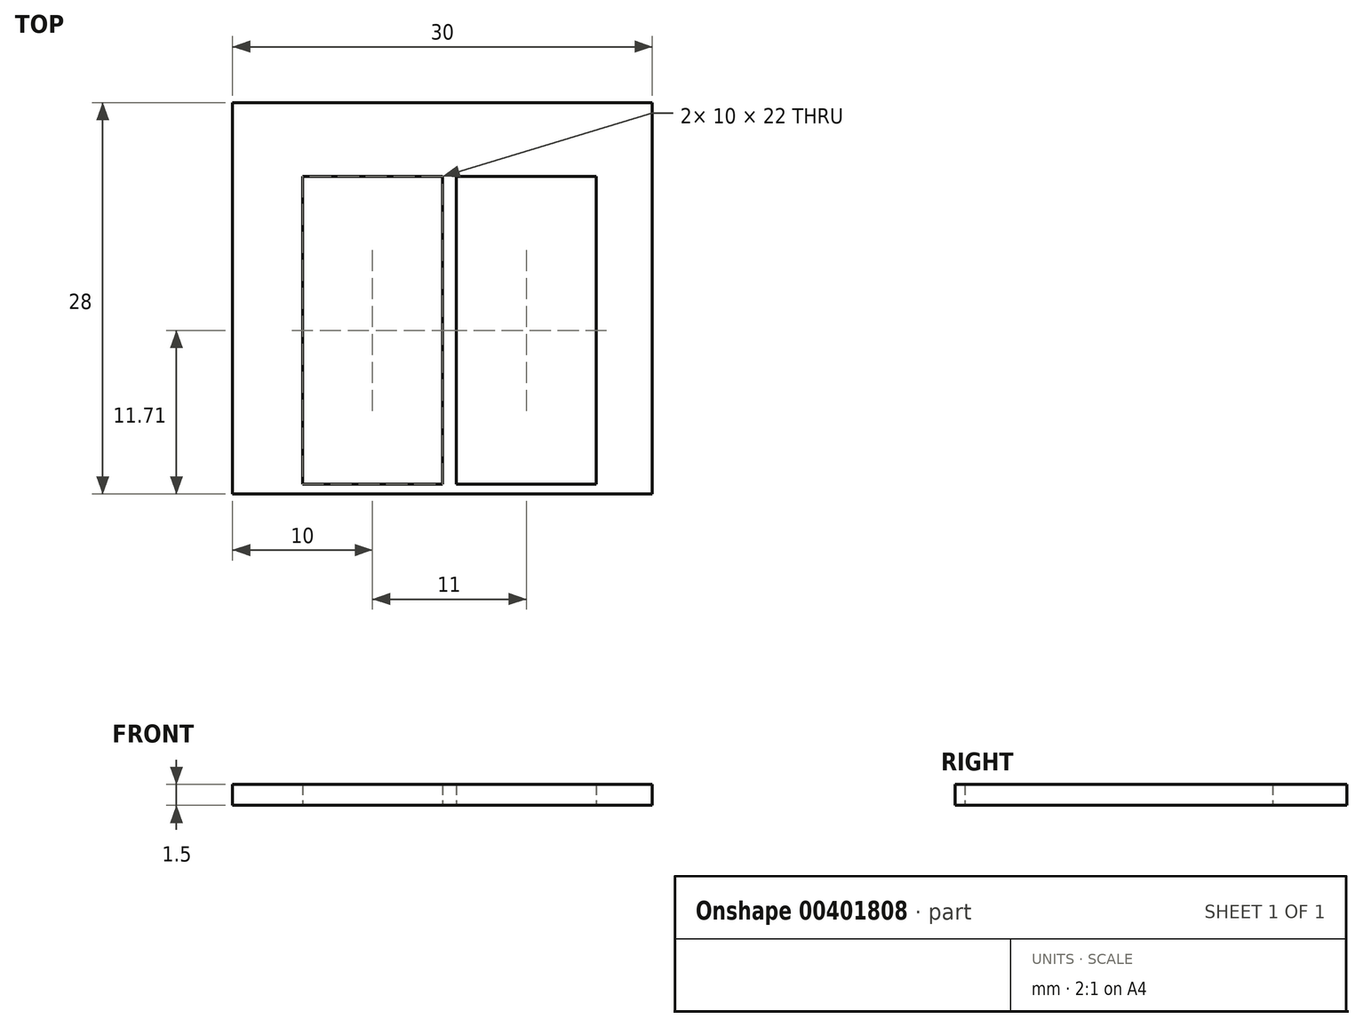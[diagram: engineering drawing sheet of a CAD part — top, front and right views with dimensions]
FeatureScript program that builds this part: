
annotation { "Feature Type Name" : "Feature", "Feature Type Description" : "" }
export const myFeature = defineFeature(function(context is Context, id is Id, definition is map)
    precondition{}
    {
        {
            var Q0;
            Q0=qCreatedBy(makeId("Top.planeOp"),FACE);
            var sketch = newSketch(context, id + "F0", { "sketchPlane" : qUnion([Q0])});
            skLineSegment(sketch, "E0.bottom", {"start": v(0, 0) * mm, "end": v(30, 0) * mm});
            skLineSegment(sketch, "E0.top", {"start": v(0, 28) * mm, "end": v(30, 28) * mm});
            skLineSegment(sketch, "E0.left", {"start": v(0, 0) * mm, "end": v(0, 28) * mm});
            skLineSegment(sketch, "E0.right", {"start": v(30, 0) * mm, "end": v(30, 28) * mm});
            skLineSegment(sketch, "E1.bottom", {"start": v(5, 22.7) * mm, "end": v(15, 22.7) * mm});
            skLineSegment(sketch, "E1.top", {"start": v(5, 0.7) * mm, "end": v(15, 0.7) * mm});
            skLineSegment(sketch, "E1.left", {"start": v(5, 22.7) * mm, "end": v(5, 0.7) * mm});
            skLineSegment(sketch, "E1.right", {"start": v(15, 22.7) * mm, "end": v(15, 0.7) * mm});
            skLineSegment(sketch, "E2.1.0.0", {"start": v(16, 22.7) * mm, "end": v(16, 0.7) * mm});
            skLineSegment(sketch, "E2.1.0.1", {"start": v(16, 22.7) * mm, "end": v(26, 22.7) * mm});
            skLineSegment(sketch, "E2.1.0.2", {"start": v(26, 22.7) * mm, "end": v(26, 0.7) * mm});
            skLineSegment(sketch, "E2.1.0.3", {"start": v(16, 0.7) * mm, "end": v(26, 0.7) * mm});
            skLineSegment(sketch, "E2.direction1", {"start": v(5, 0.7) * mm, "end": v(16, 0.7) * mm, "construction": true});
            skSolve(sketch);
        }
        {
            var Q0;
            Q0 = qSketchRegion(id + "F0", true);
            extrude(context, id + "F1", {"entities" : qUnion([Q0]), "depth" : 1.5 * mm});
        }
    });
